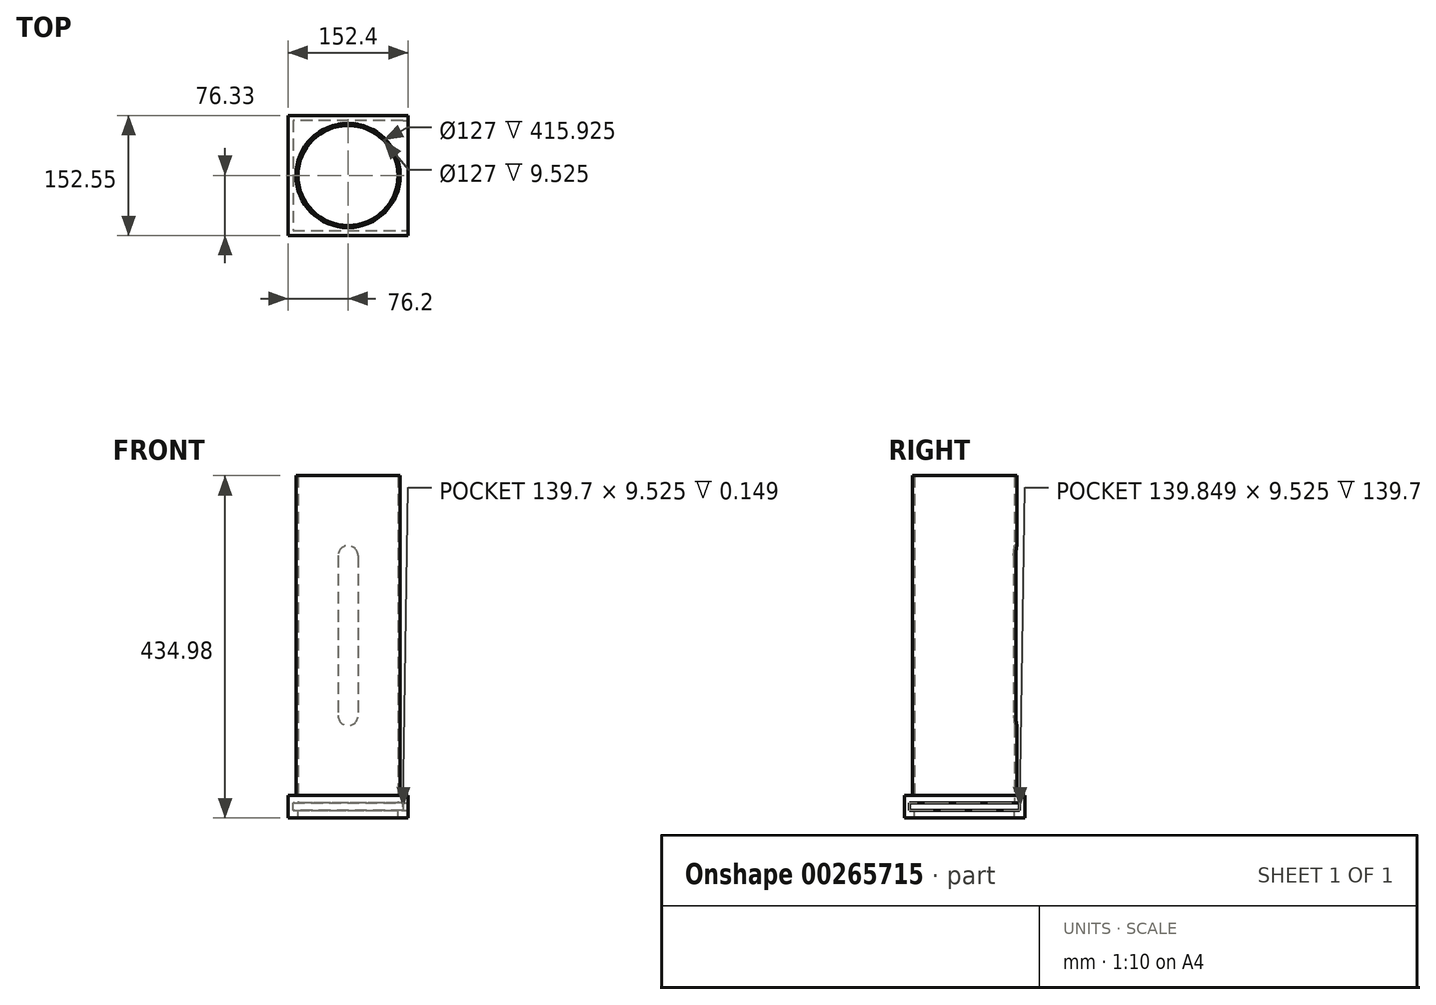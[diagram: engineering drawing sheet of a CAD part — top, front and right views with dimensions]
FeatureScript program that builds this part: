
annotation { "Feature Type Name" : "Feature", "Feature Type Description" : "" }
export const myFeature = defineFeature(function(context is Context, id is Id, definition is map)
    precondition{}
    {
        {
            var Q0;
            Q0=qCreatedBy(makeId("Top.planeOp"),FACE);
            var sketch = newSketch(context, id + "F0", { "sketchPlane" : qUnion([Q0])});
            skCircle(sketch, "E0", {"center": v(0, 0) * mm, "radius": 63.5 * mm});
            skCircle(sketch, "E1.0", {"center": v(0, 0) * mm, "radius": 66.27 * mm});
            skSolve(sketch);
        }
        {
            var Q0;
            Q0=makeQuery(id+"F0.imprint","IMPRINT",FACE,{"disambiguationData":[TD([[makeQuery(id+"F0.imprint","IMPRINT",EDGE,{"derivedFrom":sQuery(id+"F0.wireOp",EDGE,"E0")}),-1.0]])]});
            extrude(context, id + "F1", {"entities" : qUnion([Q0]), "depth" : 406.4 * mm});
        }
        {
            var Q0;
            Q0=qCreatedBy(makeId("Front.planeOp"),FACE);
            var sketch = newSketch(context, id + "F2", { "sketchPlane" : qUnion([Q0])});
            skLineSegment(sketch, "E2", {"start": v(0, 0) * mm, "end": v(0, 88.9) * mm});
            skArc(sketch, "E3", {"start": v(-12.7, 101.6) * mm, "mid": v(0, 88.9) * mm, "end": v(12.7, 101.6) * mm});
            skLineSegment(sketch, "E4", {"start": v(-12.7, 101.6) * mm, "end": v(-12.7, 203.2) * mm});
            skLineSegment(sketch, "E5", {"start": v(12.7, 203.2) * mm, "end": v(12.7, 101.6) * mm});
            skLineSegment(sketch, "E6.MirrorCS", {"start": v(12.7, 203.2) * mm, "end": v(12.7, 304.8) * mm});
            skLineSegment(sketch, "E7.MirrorCS", {"start": v(-12.7, 304.8) * mm, "end": v(-12.7, 203.2) * mm});
            skArc(sketch, "E8.MirrorCS", {"start": v(-12.7, 304.8) * mm, "mid": v(0, 317.5) * mm, "end": v(12.7, 304.8) * mm});
            skSolve(sketch);
        }
        {
            var Q0;
            Q0 = qSketchRegion(id + "F2", true);
            extrude(context, id + "F3", {"entities" : qUnion([Q0]), "operationType" : NewBodyOperationType.REMOVE, "endBound" : BoundingType.THROUGH_ALL, "oppositeDirection" : true, "depth" : 25.4 * mm});
        }
        {
            var Q0;
            Q0=qCreatedBy(makeId("Top.planeOp"),FACE);
            var sketch = newSketch(context, id + "F4", { "sketchPlane" : qUnion([Q0])});
            skLineSegment(sketch, "E9", {"start": v(-76.2, 0.02) * mm, "end": v(-76.2, 76.22) * mm});
            skLineSegment(sketch, "E10", {"start": v(-76.2, 76.22) * mm, "end": v(76.2, 76.22) * mm});
            skLineSegment(sketch, "E11", {"start": v(76.2, 76.22) * mm, "end": v(76.2, -76.33) * mm});
            skLineSegment(sketch, "E12", {"start": v(76.2, -76.33) * mm, "end": v(-76.2, -76.33) * mm});
            skLineSegment(sketch, "E13", {"start": v(-76.2, -76.33) * mm, "end": v(-76.2, 0.02) * mm});
            skSolve(sketch);
        }
        {
            var Q0;
            Q0 = qSketchRegion(id + "F4", true);
            extrude(context, id + "F5", {"entities" : qUnion([Q0]), "operationType" : NewBodyOperationType.ADD, "oppositeDirection" : true, "depth" : 9.52 * mm});
        }
        {
            var Q0;
            Q0=makeQuery(id+"F5.opExtrude","CAP_FACE",FACE,{"disambiguationData":[OSD([sQuery(id+"F4.wireOp",EDGE,"E9"),sQuery(id+"F4.wireOp",EDGE,"E10"),sQuery(id+"F4.wireOp",EDGE,"E11"),sQuery(id+"F4.wireOp",EDGE,"E12"),sQuery(id+"F4.wireOp",EDGE,"E13")])],"isStart":false});
            var sketch = newSketch(context, id + "F6", { "sketchPlane" : qUnion([Q0])});
            skLineSegment(sketch, "E14", {"start": v(-76.2, -76.22) * mm, "end": v(-76.2, 76.33) * mm});
            skLineSegment(sketch, "E15", {"start": v(-76.2, 76.33) * mm, "end": v(76.2, 76.33) * mm});
            skLineSegment(sketch, "E16", {"start": v(76.2, 76.33) * mm, "end": v(76.2, -76.22) * mm});
            skLineSegment(sketch, "E17", {"start": v(76.2, -76.22) * mm, "end": v(-76.2, -76.22) * mm});
            skLineSegment(sketch, "E18.0", {"start": v(-69.85, -69.87) * mm, "end": v(-69.85, 69.98) * mm});
            skLineSegment(sketch, "E18.1", {"start": v(69.85, -69.87) * mm, "end": v(-69.85, -69.87) * mm});
            skLineSegment(sketch, "E18.2", {"start": v(69.85, 69.98) * mm, "end": v(69.85, -69.87) * mm});
            skLineSegment(sketch, "E18.3", {"start": v(-69.85, 69.98) * mm, "end": v(69.85, 69.98) * mm});
            skSolve(sketch);
        }
        {
            var Q0;
            Q0 = qSketchRegion(id + "F6", true);
            extrude(context, id + "F7", {"entities" : qUnion([Q0]), "operationType" : NewBodyOperationType.ADD, "depth" : 9.52 * mm});
        }
        {
            var Q0;
            Q0=makeQuery(id+"F7.opExtrude","CAP_FACE",FACE,{"disambiguationData":[OSD([sQuery(id+"F6.wireOp",EDGE,"E14"),sQuery(id+"F6.wireOp",EDGE,"E15"),sQuery(id+"F6.wireOp",EDGE,"E16"),sQuery(id+"F6.wireOp",EDGE,"E17"),sQuery(id+"F6.wireOp",EDGE,"E18.0"),sQuery(id+"F6.wireOp",EDGE,"E18.1"),sQuery(id+"F6.wireOp",EDGE,"E18.2"),sQuery(id+"F6.wireOp",EDGE,"E18.3")])],"isStart":false});
            var sketch = newSketch(context, id + "F8", { "sketchPlane" : qUnion([Q0])});
            skLineSegment(sketch, "E19", {"start": v(-76.2, 76.33) * mm, "end": v(76.2, 76.33) * mm});
            skLineSegment(sketch, "E20", {"start": v(76.2, 76.33) * mm, "end": v(76.2, -76.22) * mm});
            skLineSegment(sketch, "E21", {"start": v(76.2, -76.22) * mm, "end": v(-76.2, -76.22) * mm});
            skLineSegment(sketch, "E22", {"start": v(-76.2, -76.22) * mm, "end": v(-76.2, 76.33) * mm});
            skSolve(sketch);
        }
        {
            var Q0;
            Q0 = qSketchRegion(id + "F8", true);
            extrude(context, id + "F9", {"entities" : qUnion([Q0]), "operationType" : NewBodyOperationType.ADD, "depth" : 9.52 * mm});
        }
        {
            var Q0;
            Q0=makeQuery(id+"F5.boolean.opBoolean","SPLIT",FACE,{"disambiguationData":[TD([makeQuery(id+"F1.opExtrude","SWEPT_FACE",FACE,{"disambiguationData":[OSD([sQuery(id+"F0.wireOp",EDGE,"E0")])]})])],"derivedFrom":makeQuery(id+"F5.opExtrude","CAP_FACE",FACE,{"disambiguationData":[OSD([sQuery(id+"F4.wireOp",EDGE,"E9"),sQuery(id+"F4.wireOp",EDGE,"E10"),sQuery(id+"F4.wireOp",EDGE,"E11"),sQuery(id+"F4.wireOp",EDGE,"E12"),sQuery(id+"F4.wireOp",EDGE,"E13")])],"isStart":true})});
            extrude(context, id + "F10", {"entities" : qUnion([Q0]), "operationType" : NewBodyOperationType.REMOVE, "endBound" : BoundingType.THROUGH_ALL, "oppositeDirection" : true, "depth" : 25.4 * mm});
        }
        {
            var Q0;
            Q0=makeQuery(id+"F9.boolean.opBoolean","MERGE",FACE,{"derivedFrom":[makeQuery(id+"F7.boolean.opBoolean","MERGE",FACE,{"derivedFrom":[makeQuery(id+"F5.opExtrude","SWEPT_FACE",FACE,{"disambiguationData":[OSD([sQuery(id+"F4.wireOp",EDGE,"E11")])]}),makeQuery(id+"F7.opExtrude","SWEPT_FACE",FACE,{"disambiguationData":[OSD([sQuery(id+"F6.wireOp",EDGE,"E16")])]})]}),makeQuery(id+"F9.opExtrude","SWEPT_FACE",FACE,{"disambiguationData":[OSD([sQuery(id+"F8.wireOp",EDGE,"E20")])]})]});
            var sketch = newSketch(context, id + "F11", { "sketchPlane" : qUnion([Q0])});
            skLineSegment(sketch, "E23", {"start": v(69.72, -9.52) * mm, "end": v(69.72, -19.05) * mm});
            skLineSegment(sketch, "E24", {"start": v(69.72, -19.05) * mm, "end": v(-69.98, -19.05) * mm});
            skLineSegment(sketch, "E25", {"start": v(-69.98, -19.05) * mm, "end": v(-69.98, -9.53) * mm});
            skLineSegment(sketch, "E26", {"start": v(-69.98, -9.53) * mm, "end": v(69.72, -9.52) * mm});
            skSolve(sketch);
        }
        {
            var Q0;
            Q0 = qSketchRegion(id + "F11", true);
            extrude(context, id + "F12", {"entities" : qUnion([Q0]), "operationType" : NewBodyOperationType.REMOVE, "oppositeDirection" : true, "depth" : 25.4 * mm});
        }
    });
